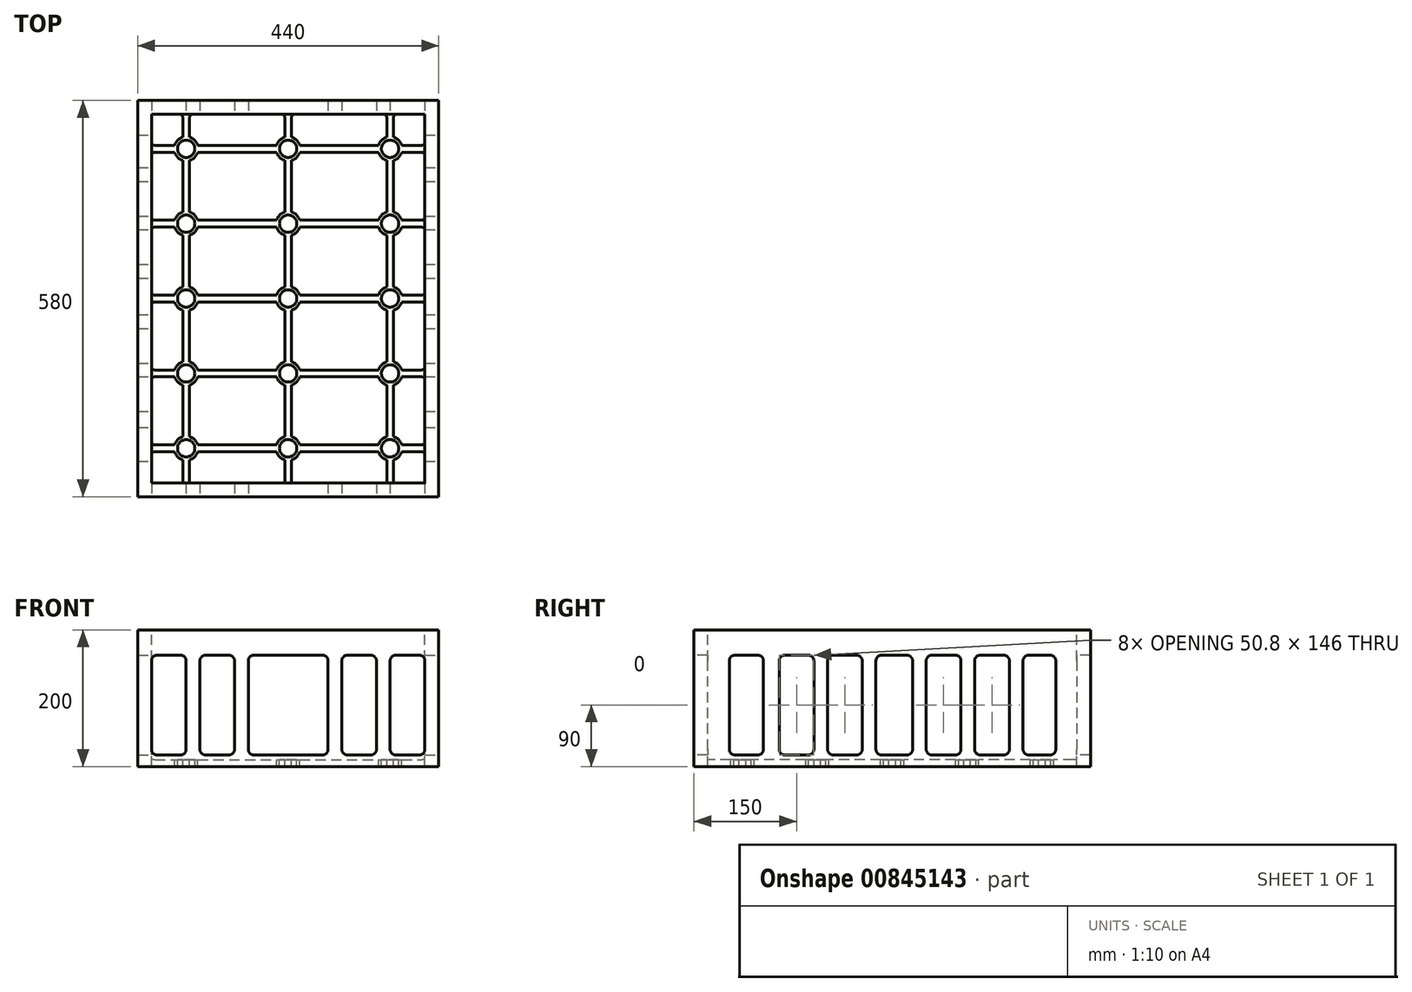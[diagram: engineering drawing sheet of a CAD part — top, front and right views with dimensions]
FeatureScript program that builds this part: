
annotation { "Feature Type Name" : "Feature", "Feature Type Description" : "" }
export const myFeature = defineFeature(function(context is Context, id is Id, definition is map)
    precondition{}
    {
        {
            var Q0;
            Q0=qCreatedBy(makeId("Top.planeOp"),FACE);
            var sketch = newSketch(context, id + "F0", { "sketchPlane" : qUnion([Q0])});
            skLineSegment(sketch, "E0.bottom", {"start": v(0, 0) * mm, "end": v(440, 0) * mm});
            skLineSegment(sketch, "E0.top", {"start": v(0, 580) * mm, "end": v(440, 580) * mm});
            skLineSegment(sketch, "E0.left", {"start": v(0, 0) * mm, "end": v(0, 580) * mm});
            skLineSegment(sketch, "E0.right", {"start": v(440, 0) * mm, "end": v(440, 580) * mm});
            skSolve(sketch);
        }
        {
            var Q0;
            Q0 = qSketchRegion(id + "F0", true);
            extrude(context, id + "F1", {"entities" : qUnion([Q0]), "depth" : 200 * mm, "offsetDistance" : 25 * mm});
        }
        {
            var Q0;
            Q0=makeQuery(id+"F1.opExtrude","CAP_FACE",FACE,{"disambiguationData":[OSD([sQuery(id+"F0.wireOp",EDGE,"E0.bottom"),sQuery(id+"F0.wireOp",EDGE,"E0.top"),sQuery(id+"F0.wireOp",EDGE,"E0.left"),sQuery(id+"F0.wireOp",EDGE,"E0.right")])],"isStart":false});
            var sketch = newSketch(context, id + "F2", { "sketchPlane" : qUnion([Q0])});
            skLineSegment(sketch, "E1.left", {"start": v(0, 0) * mm, "end": v(0, 0) * mm});
            skLineSegment(sketch, "E2.bottom", {"start": v(20, 20) * mm, "end": v(420, 20) * mm});
            skLineSegment(sketch, "E2.top", {"start": v(20, 560) * mm, "end": v(420, 560) * mm});
            skLineSegment(sketch, "E2.left", {"start": v(20, 20) * mm, "end": v(20, 560) * mm});
            skLineSegment(sketch, "E2.right", {"start": v(420, 20) * mm, "end": v(420, 560) * mm});
            skSolve(sketch);
        }
        {
            var Q0;
            Q0=makeQuery(id+"F2.imprint","IMPRINT",FACE,{"disambiguationData":[TD([[makeQuery(id+"F2.imprint","IMPRINT",EDGE,{"derivedFrom":sQuery(id+"F2.wireOp",EDGE,"E2.bottom")}),1.0]])]});
            extrude(context, id + "F3", {"entities" : qUnion([Q0]), "operationType" : NewBodyOperationType.REMOVE, "oppositeDirection" : true, "depth" : 190 * mm, "offsetDistance" : 25 * mm});
        }
        {
            var Q0;
            Q0=makeQuery(id+"F3.boolean.opBoolean","COPY",FACE,{"derivedFrom":makeQuery(id+"F3.opExtrude","CAP_FACE",FACE,{"disambiguationData":[OSD([sQuery(id+"F2.wireOp",EDGE,"E2.bottom"),sQuery(id+"F2.wireOp",EDGE,"E2.top"),sQuery(id+"F2.wireOp",EDGE,"E2.left"),sQuery(id+"F2.wireOp",EDGE,"E2.right")])],"isStart":false})});
            var sketch = newSketch(context, id + "F4", { "sketchPlane" : qUnion([Q0])});
            skCircle(sketch, "E3", {"center": v(70.8, 509.2) * mm, "radius": 12.7 * mm});
            skCircle(sketch, "E4", {"center": v(70.8, 509.2) * mm, "radius": 17.7 * mm});
            skCircle(sketch, "E5.1.0.0", {"center": v(220, 509.2) * mm, "radius": 17.7 * mm});
            skCircle(sketch, "E5.1.0.1", {"center": v(220, 509.2) * mm, "radius": 12.7 * mm});
            skCircle(sketch, "E5.2.0.0", {"center": v(369.2, 509.2) * mm, "radius": 17.7 * mm});
            skCircle(sketch, "E5.2.0.1", {"center": v(369.2, 509.2) * mm, "radius": 12.7 * mm});
            skCircle(sketch, "E6.0.1.0", {"center": v(369.2, 399.6) * mm, "radius": 17.7 * mm});
            skCircle(sketch, "E6.0.1.1", {"center": v(70.8, 399.6) * mm, "radius": 12.7 * mm});
            skCircle(sketch, "E6.0.1.2", {"center": v(369.2, 399.6) * mm, "radius": 12.7 * mm});
            skArc(sketch, "E6.0.1.3", {"start": v(87.78, 404.6) * mm, "mid": v(53.1, 399.6) * mm, "end": v(87.78, 394.6) * mm});
            skCircle(sketch, "E6.0.1.4", {"center": v(220, 399.6) * mm, "radius": 17.7 * mm});
            skCircle(sketch, "E6.0.1.5", {"center": v(220, 399.6) * mm, "radius": 12.7 * mm});
            skCircle(sketch, "E6.0.2.0", {"center": v(369.2, 290) * mm, "radius": 17.7 * mm});
            skCircle(sketch, "E6.0.2.1", {"center": v(70.8, 290) * mm, "radius": 12.7 * mm});
            skCircle(sketch, "E6.0.2.2", {"center": v(369.2, 290) * mm, "radius": 12.7 * mm});
            skCircle(sketch, "E6.0.2.3", {"center": v(70.8, 290) * mm, "radius": 17.7 * mm});
            skCircle(sketch, "E6.0.2.4", {"center": v(220, 290) * mm, "radius": 17.7 * mm});
            skCircle(sketch, "E6.0.2.5", {"center": v(220, 290) * mm, "radius": 12.7 * mm});
            skCircle(sketch, "E6.0.3.0", {"center": v(369.2, 180.4) * mm, "radius": 17.7 * mm});
            skCircle(sketch, "E6.0.3.1", {"center": v(70.8, 180.4) * mm, "radius": 12.7 * mm});
            skCircle(sketch, "E6.0.3.2", {"center": v(369.2, 180.4) * mm, "radius": 12.7 * mm});
            skCircle(sketch, "E6.0.3.3", {"center": v(70.8, 180.4) * mm, "radius": 17.7 * mm});
            skCircle(sketch, "E6.0.3.4", {"center": v(220, 180.4) * mm, "radius": 17.7 * mm});
            skCircle(sketch, "E6.0.3.5", {"center": v(220, 180.4) * mm, "radius": 12.7 * mm});
            skCircle(sketch, "E6.0.4.0", {"center": v(369.2, 70.8) * mm, "radius": 17.7 * mm});
            skCircle(sketch, "E6.0.4.1", {"center": v(70.8, 70.8) * mm, "radius": 12.7 * mm});
            skCircle(sketch, "E6.0.4.2", {"center": v(369.2, 70.8) * mm, "radius": 12.7 * mm});
            skCircle(sketch, "E6.0.4.3", {"center": v(70.8, 70.8) * mm, "radius": 17.7 * mm});
            skCircle(sketch, "E6.0.4.4", {"center": v(220, 70.8) * mm, "radius": 17.7 * mm});
            skCircle(sketch, "E6.0.4.5", {"center": v(220, 70.8) * mm, "radius": 12.7 * mm});
            skLineSegment(sketch, "E7.0", {"start": v(25, 504.2) * mm, "end": v(53.82, 504.2) * mm});
            skLineSegment(sketch, "E8.0", {"start": v(25, 514.2) * mm, "end": v(53.82, 514.2) * mm});
            skLineSegment(sketch, "E9.bottom", {"start": v(20, 20) * mm, "end": v(420, 20) * mm});
            skLineSegment(sketch, "E9.top", {"start": v(80.8, 560) * mm, "end": v(210, 560) * mm});
            skLineSegment(sketch, "E9.left", {"start": v(20, 519.2) * mm, "end": v(20, 560) * mm});
            skLineSegment(sketch, "E9.right", {"start": v(420, 409.6) * mm, "end": v(420, 499.2) * mm});
            skArc(sketch, "E10.filletArc", {"start": v(20, 519.2) * mm, "mid": v(21.46, 515.66) * mm, "end": v(25, 514.2) * mm});
            skLineSegment(sketch, "E11", {"start": v(20, 389.6) * mm, "end": v(20, 300) * mm});
            skPoint(sketch, "E12.visualSharp", {"position": v(20, 504.2) * mm});
            skArc(sketch, "E12.filletArc", {"start": v(25, 504.2) * mm, "mid": v(21.46, 502.74) * mm, "end": v(20, 499.2) * mm});
            skLineSegment(sketch, "E13.0", {"start": v(65.8, 555) * mm, "end": v(65.8, 526.18) * mm});
            skLineSegment(sketch, "E14.0", {"start": v(75.8, 555) * mm, "end": v(75.8, 526.18) * mm});
            skLineSegment(sketch, "E15", {"start": v(20, 560) * mm, "end": v(60.8, 560) * mm});
            skArc(sketch, "E16.filletArc", {"start": v(80.8, 560) * mm, "mid": v(77.26, 558.54) * mm, "end": v(75.8, 555) * mm});
            skArc(sketch, "E17.filletArc", {"start": v(65.8, 555) * mm, "mid": v(64.34, 558.54) * mm, "end": v(60.8, 560) * mm});
            skLineSegment(sketch, "E18.trimOffspring", {"start": v(87.78, 514.2) * mm, "end": v(203.02, 514.2) * mm});
            skLineSegment(sketch, "E19.trimOffspring", {"start": v(87.78, 504.2) * mm, "end": v(203.02, 504.2) * mm});
            skLineSegment(sketch, "E20.trimOffspring", {"start": v(65.8, 492.22) * mm, "end": v(65.8, 416.58) * mm});
            skLineSegment(sketch, "E21.trimOffspring", {"start": v(75.8, 492.22) * mm, "end": v(75.8, 416.58) * mm});
            skLineSegment(sketch, "E22.0", {"start": v(215, 555) * mm, "end": v(215, 526.18) * mm});
            skLineSegment(sketch, "E23.0", {"start": v(225, 555) * mm, "end": v(225, 526.18) * mm});
            skLineSegment(sketch, "E24.0", {"start": v(364.2, 555) * mm, "end": v(364.2, 526.18) * mm});
            skLineSegment(sketch, "E25.0", {"start": v(374.2, 555) * mm, "end": v(374.2, 526.18) * mm});
            skArc(sketch, "E26.filletArc", {"start": v(215, 555) * mm, "mid": v(213.54, 558.54) * mm, "end": v(210, 560) * mm});
            skLineSegment(sketch, "E27", {"start": v(379.2, 560) * mm, "end": v(420, 560) * mm});
            skPoint(sketch, "E28.visualSharp", {"position": v(225, 560) * mm});
            skArc(sketch, "E28.filletArc", {"start": v(230, 560) * mm, "mid": v(226.46, 558.54) * mm, "end": v(225, 555) * mm});
            skArc(sketch, "E29.filletArc", {"start": v(379.2, 560) * mm, "mid": v(375.66, 558.54) * mm, "end": v(374.2, 555) * mm});
            skLineSegment(sketch, "E30", {"start": v(230, 560) * mm, "end": v(359.2, 560) * mm});
            skPoint(sketch, "E31.visualSharp", {"position": v(364.2, 560) * mm});
            skArc(sketch, "E31.filletArc", {"start": v(364.2, 555) * mm, "mid": v(362.74, 558.54) * mm, "end": v(359.2, 560) * mm});
            skArc(sketch, "E32.filletArc", {"start": v(420, 499.2) * mm, "mid": v(418.54, 502.74) * mm, "end": v(415, 504.2) * mm});
            skLineSegment(sketch, "E33", {"start": v(420, 560) * mm, "end": v(420, 519.2) * mm});
            skPoint(sketch, "E34.visualSharp", {"position": v(420, 514.2) * mm});
            skArc(sketch, "E34.filletArc", {"start": v(415, 514.2) * mm, "mid": v(418.54, 515.66) * mm, "end": v(420, 519.2) * mm});
            skLineSegment(sketch, "E35.0", {"start": v(25, 394.6) * mm, "end": v(53.82, 394.6) * mm});
            skLineSegment(sketch, "E36.0", {"start": v(25, 404.6) * mm, "end": v(53.82, 404.6) * mm});
            skArc(sketch, "E37.filletArc", {"start": v(25, 394.6) * mm, "mid": v(21.46, 393.14) * mm, "end": v(20, 389.6) * mm});
            skLineSegment(sketch, "E38", {"start": v(20, 499.2) * mm, "end": v(20, 409.6) * mm});
            skPoint(sketch, "E39.visualSharp", {"position": v(20, 404.6) * mm});
            skArc(sketch, "E39.filletArc", {"start": v(20, 409.6) * mm, "mid": v(21.46, 406.06) * mm, "end": v(25, 404.6) * mm});
            skArc(sketch, "E40.filletArc", {"start": v(415, 404.6) * mm, "mid": v(418.54, 406.06) * mm, "end": v(420, 409.6) * mm});
            skLineSegment(sketch, "E41", {"start": v(420, 389.6) * mm, "end": v(420, 300) * mm});
            skPoint(sketch, "E42.visualSharp", {"position": v(420, 394.6) * mm});
            skArc(sketch, "E42.filletArc", {"start": v(420, 389.6) * mm, "mid": v(418.54, 393.14) * mm, "end": v(415, 394.6) * mm});
            skLineSegment(sketch, "E43.trimOffspring", {"start": v(215, 492.22) * mm, "end": v(215, 416.58) * mm});
            skLineSegment(sketch, "E44.trimOffspring", {"start": v(225, 492.22) * mm, "end": v(225, 416.58) * mm});
            skLineSegment(sketch, "E45.trimOffspring", {"start": v(236.98, 504.2) * mm, "end": v(352.22, 504.2) * mm});
            skLineSegment(sketch, "E46.trimOffspring", {"start": v(236.98, 514.2) * mm, "end": v(352.22, 514.2) * mm});
            skLineSegment(sketch, "E47.trimOffspring", {"start": v(364.2, 492.22) * mm, "end": v(364.2, 416.58) * mm});
            skLineSegment(sketch, "E48.trimOffspring", {"start": v(374.2, 492.22) * mm, "end": v(374.2, 416.58) * mm});
            skLineSegment(sketch, "E49.trimOffspring", {"start": v(386.18, 504.2) * mm, "end": v(415, 504.2) * mm});
            skLineSegment(sketch, "E50.trimOffspring", {"start": v(386.18, 514.2) * mm, "end": v(415, 514.2) * mm});
            skLineSegment(sketch, "E51.trimOffspring", {"start": v(87.78, 404.6) * mm, "end": v(203.02, 404.6) * mm});
            skLineSegment(sketch, "E52.trimOffspring", {"start": v(87.78, 394.6) * mm, "end": v(203.02, 394.6) * mm});
            skLineSegment(sketch, "E53.trimOffspring", {"start": v(75.8, 382.62) * mm, "end": v(75.8, 306.98) * mm});
            skLineSegment(sketch, "E54.trimOffspring", {"start": v(65.8, 382.62) * mm, "end": v(65.8, 306.98) * mm});
            skLineSegment(sketch, "E55.trimOffspring", {"start": v(215, 382.62) * mm, "end": v(215, 306.98) * mm});
            skLineSegment(sketch, "E56.trimOffspring", {"start": v(225, 382.62) * mm, "end": v(225, 306.98) * mm});
            skLineSegment(sketch, "E57.trimOffspring", {"start": v(236.98, 394.6) * mm, "end": v(352.22, 394.6) * mm});
            skLineSegment(sketch, "E58.trimOffspring", {"start": v(236.98, 404.6) * mm, "end": v(352.22, 404.6) * mm});
            skLineSegment(sketch, "E59.trimOffspring", {"start": v(364.2, 382.62) * mm, "end": v(364.2, 306.98) * mm});
            skLineSegment(sketch, "E60.trimOffspring", {"start": v(374.2, 382.62) * mm, "end": v(374.2, 306.98) * mm});
            skLineSegment(sketch, "E61.trimOffspring", {"start": v(386.18, 394.6) * mm, "end": v(415, 394.6) * mm});
            skLineSegment(sketch, "E62.trimOffspring", {"start": v(386.18, 404.6) * mm, "end": v(415, 404.6) * mm});
            skLineSegment(sketch, "E63.0", {"start": v(25, 285) * mm, "end": v(53.82, 285) * mm});
            skLineSegment(sketch, "E64.0", {"start": v(25, 295) * mm, "end": v(53.82, 295) * mm});
            skArc(sketch, "E65.filletArc", {"start": v(20, 300) * mm, "mid": v(21.46, 296.46) * mm, "end": v(25, 295) * mm});
            skArc(sketch, "E66.filletArc", {"start": v(415, 295) * mm, "mid": v(418.54, 296.46) * mm, "end": v(420, 300) * mm});
            skLineSegment(sketch, "E67", {"start": v(20, 280) * mm, "end": v(20, 190.4) * mm});
            skLineSegment(sketch, "E68", {"start": v(420, 280) * mm, "end": v(420, 190.4) * mm});
            skPoint(sketch, "E69.visualSharp", {"position": v(20, 285) * mm});
            skArc(sketch, "E69.filletArc", {"start": v(25, 285) * mm, "mid": v(21.46, 283.54) * mm, "end": v(20, 280) * mm});
            skPoint(sketch, "E70.visualSharp", {"position": v(420, 285) * mm});
            skArc(sketch, "E70.filletArc", {"start": v(420, 280) * mm, "mid": v(418.54, 283.54) * mm, "end": v(415, 285) * mm});
            skLineSegment(sketch, "E71.trimOffspring", {"start": v(65.8, 273.02) * mm, "end": v(65.8, 197.38) * mm});
            skLineSegment(sketch, "E72.trimOffspring", {"start": v(75.8, 273.02) * mm, "end": v(75.8, 197.38) * mm});
            skLineSegment(sketch, "E73.trimOffspring", {"start": v(87.78, 285) * mm, "end": v(203.02, 285) * mm});
            skLineSegment(sketch, "E74.trimOffspring", {"start": v(87.78, 295) * mm, "end": v(203.02, 295) * mm});
            skLineSegment(sketch, "E75.trimOffspring", {"start": v(215, 273.02) * mm, "end": v(215, 197.38) * mm});
            skLineSegment(sketch, "E76.trimOffspring", {"start": v(225, 273.02) * mm, "end": v(225, 197.38) * mm});
            skLineSegment(sketch, "E77.trimOffspring", {"start": v(236.98, 285) * mm, "end": v(352.22, 285) * mm});
            skLineSegment(sketch, "E78.trimOffspring", {"start": v(236.98, 295) * mm, "end": v(352.22, 295) * mm});
            skLineSegment(sketch, "E79.trimOffspring", {"start": v(364.2, 273.02) * mm, "end": v(364.2, 197.38) * mm});
            skLineSegment(sketch, "E80.trimOffspring", {"start": v(374.2, 273.02) * mm, "end": v(374.2, 197.38) * mm});
            skLineSegment(sketch, "E81.trimOffspring", {"start": v(386.18, 285) * mm, "end": v(415, 285) * mm});
            skLineSegment(sketch, "E82.trimOffspring", {"start": v(386.18, 295) * mm, "end": v(415, 295) * mm});
            skLineSegment(sketch, "E83.0", {"start": v(25, 175.4) * mm, "end": v(53.82, 175.4) * mm});
            skLineSegment(sketch, "E84.0", {"start": v(25, 185.4) * mm, "end": v(53.82, 185.4) * mm});
            skArc(sketch, "E85.filletArc", {"start": v(20, 190.4) * mm, "mid": v(21.46, 186.86) * mm, "end": v(25, 185.4) * mm});
            skArc(sketch, "E86.filletArc", {"start": v(415, 185.4) * mm, "mid": v(418.54, 186.86) * mm, "end": v(420, 190.4) * mm});
            skLineSegment(sketch, "E87", {"start": v(20, 170.4) * mm, "end": v(20, 80.8) * mm});
            skLineSegment(sketch, "E88", {"start": v(420, 170.4) * mm, "end": v(420, 80.8) * mm});
            skPoint(sketch, "E89.visualSharp", {"position": v(20, 175.4) * mm});
            skArc(sketch, "E89.filletArc", {"start": v(25, 175.4) * mm, "mid": v(21.46, 173.94) * mm, "end": v(20, 170.4) * mm});
            skPoint(sketch, "E90.visualSharp", {"position": v(420, 175.4) * mm});
            skArc(sketch, "E90.filletArc", {"start": v(420, 170.4) * mm, "mid": v(418.54, 173.94) * mm, "end": v(415, 175.4) * mm});
            skLineSegment(sketch, "E91.trimOffspring", {"start": v(75.8, 163.42) * mm, "end": v(75.8, 87.78) * mm});
            skLineSegment(sketch, "E92.trimOffspring", {"start": v(65.8, 163.42) * mm, "end": v(65.8, 87.78) * mm});
            skLineSegment(sketch, "E93.trimOffspring", {"start": v(87.78, 175.4) * mm, "end": v(203.02, 175.4) * mm});
            skLineSegment(sketch, "E94.trimOffspring", {"start": v(87.78, 185.4) * mm, "end": v(203.02, 185.4) * mm});
            skLineSegment(sketch, "E95.trimOffspring", {"start": v(215, 163.42) * mm, "end": v(215, 87.78) * mm});
            skLineSegment(sketch, "E96.trimOffspring", {"start": v(225, 163.42) * mm, "end": v(225, 87.78) * mm});
            skLineSegment(sketch, "E97.trimOffspring", {"start": v(236.98, 175.4) * mm, "end": v(352.22, 175.4) * mm});
            skLineSegment(sketch, "E98.trimOffspring", {"start": v(236.98, 185.4) * mm, "end": v(352.22, 185.4) * mm});
            skLineSegment(sketch, "E99.trimOffspring", {"start": v(364.2, 163.42) * mm, "end": v(364.2, 87.78) * mm});
            skLineSegment(sketch, "E100.trimOffspring", {"start": v(374.2, 163.42) * mm, "end": v(374.2, 87.78) * mm});
            skLineSegment(sketch, "E101.trimOffspring", {"start": v(386.18, 175.4) * mm, "end": v(415, 175.4) * mm});
            skLineSegment(sketch, "E102.trimOffspring", {"start": v(386.18, 185.4) * mm, "end": v(415, 185.4) * mm});
            skLineSegment(sketch, "E103.0", {"start": v(25, 65.8) * mm, "end": v(53.82, 65.8) * mm});
            skLineSegment(sketch, "E104.0", {"start": v(25, 75.8) * mm, "end": v(53.82, 75.8) * mm});
            skArc(sketch, "E105.filletArc", {"start": v(20, 80.8) * mm, "mid": v(21.46, 77.26) * mm, "end": v(25, 75.8) * mm});
            skArc(sketch, "E106.filletArc", {"start": v(415, 75.8) * mm, "mid": v(418.54, 77.26) * mm, "end": v(420, 80.8) * mm});
            skLineSegment(sketch, "E107", {"start": v(20, 60.8) * mm, "end": v(20, 20) * mm});
            skLineSegment(sketch, "E108", {"start": v(420, 60.8) * mm, "end": v(420, 20) * mm});
            skPoint(sketch, "E109.visualSharp", {"position": v(20, 65.8) * mm});
            skArc(sketch, "E109.filletArc", {"start": v(25, 65.8) * mm, "mid": v(21.46, 64.34) * mm, "end": v(20, 60.8) * mm});
            skPoint(sketch, "E110.visualSharp", {"position": v(420, 65.8) * mm});
            skArc(sketch, "E110.filletArc", {"start": v(420, 60.8) * mm, "mid": v(418.54, 64.34) * mm, "end": v(415, 65.8) * mm});
            skLineSegment(sketch, "E111.trimOffspring", {"start": v(65.8, 53.82) * mm, "end": v(65.8, 20) * mm});
            skLineSegment(sketch, "E112.trimOffspring", {"start": v(75.8, 53.82) * mm, "end": v(75.8, 20) * mm});
            skLineSegment(sketch, "E113.trimOffspring", {"start": v(87.78, 65.8) * mm, "end": v(203.02, 65.8) * mm});
            skLineSegment(sketch, "E114.trimOffspring", {"start": v(87.78, 75.8) * mm, "end": v(203.02, 75.8) * mm});
            skLineSegment(sketch, "E115.trimOffspring", {"start": v(215, 53.82) * mm, "end": v(215, 20) * mm});
            skLineSegment(sketch, "E116.trimOffspring", {"start": v(225, 53.82) * mm, "end": v(225, 20) * mm});
            skLineSegment(sketch, "E117.trimOffspring", {"start": v(236.98, 65.8) * mm, "end": v(352.22, 65.8) * mm});
            skLineSegment(sketch, "E118.trimOffspring", {"start": v(236.98, 75.8) * mm, "end": v(352.22, 75.8) * mm});
            skLineSegment(sketch, "E119.trimOffspring", {"start": v(364.2, 53.82) * mm, "end": v(364.2, 20) * mm});
            skLineSegment(sketch, "E120.trimOffspring", {"start": v(374.2, 53.82) * mm, "end": v(374.2, 20) * mm});
            skLineSegment(sketch, "E121.trimOffspring", {"start": v(386.18, 65.8) * mm, "end": v(415, 65.8) * mm});
            skLineSegment(sketch, "E122.trimOffspring", {"start": v(386.18, 75.8) * mm, "end": v(415, 75.8) * mm});
            skSolve(sketch);
        }
        {
            var Q0;
            {var subQ0=sQuery(id+"F4.wireOp",EDGE,"E8.0");Q0=makeQuery(id+"F4.imprint","IMPRINT",FACE,{"disambiguationData":[TD([[makeQuery(id+"F4.imprint","IMPRINT",EDGE,{"derivedFrom":subQ0}),1.0]])]});}
            var Q1;
            Q1=makeQuery(id+"F4.imprint","IMPRINT",FACE,{"disambiguationData":[TD([[makeQuery(id+"F4.imprint","IMPRINT",EDGE,{"derivedFrom":sQuery(id+"F4.wireOp",EDGE,"E9.top")}),-1.0]])]});
            var Q2;
            {var subQ3=sQuery(id+"F4.wireOp",EDGE,"E23.0");Q2=makeQuery(id+"F4.imprint","IMPRINT",FACE,{"disambiguationData":[TD([[makeQuery(id+"F4.imprint","IMPRINT",EDGE,{"derivedFrom":subQ3}),1.0]])]});}
            var Q3;
            {var subQ0=sQuery(id+"F4.wireOp",EDGE,"E25.0");Q3=makeQuery(id+"F4.imprint","IMPRINT",FACE,{"disambiguationData":[TD([[makeQuery(id+"F4.imprint","IMPRINT",EDGE,{"derivedFrom":subQ0}),1.0]])]});}
            var Q4;
            {var subQ0=sQuery(id+"F4.wireOp",EDGE,"E7.0");Q4=makeQuery(id+"F4.imprint","IMPRINT",FACE,{"disambiguationData":[TD([[makeQuery(id+"F4.imprint","IMPRINT",EDGE,{"derivedFrom":subQ0}),-1.0]])]});}
            var Q5;
            {var subQ3=sQuery(id+"F4.wireOp",EDGE,"E19.trimOffspring");Q5=makeQuery(id+"F4.imprint","IMPRINT",FACE,{"disambiguationData":[TD([[makeQuery(id+"F4.imprint","IMPRINT",EDGE,{"derivedFrom":subQ3}),-1.0]])]});}
            var Q6;
            {var subQ0=sQuery(id+"F4.wireOp",EDGE,"E44.trimOffspring");Q6=makeQuery(id+"F4.imprint","IMPRINT",FACE,{"disambiguationData":[TD([[makeQuery(id+"F4.imprint","IMPRINT",EDGE,{"derivedFrom":subQ0}),1.0]])]});}
            var Q7;
            Q7=makeQuery(id+"F4.imprint","IMPRINT",FACE,{"disambiguationData":[TD([[makeQuery(id+"F4.imprint","IMPRINT",EDGE,{"derivedFrom":sQuery(id+"F4.wireOp",EDGE,"E9.right")}),1.0]])]});
            var Q8;
            Q8=makeQuery(id+"F4.imprint","IMPRINT",FACE,{"disambiguationData":[TD([[makeQuery(id+"F4.imprint","IMPRINT",EDGE,{"derivedFrom":sQuery(id+"F4.wireOp",EDGE,"E11")}),-1.0]])]});
            var Q9;
            {var subQ5=sQuery(id+"F4.wireOp",EDGE,"E52.trimOffspring");Q9=makeQuery(id+"F4.imprint","IMPRINT",FACE,{"disambiguationData":[TD([[makeQuery(id+"F4.imprint","IMPRINT",EDGE,{"derivedFrom":subQ5}),-1.0]])]});}
            var Q10;
            {var subQ3=sQuery(id+"F4.wireOp",EDGE,"E56.trimOffspring");Q10=makeQuery(id+"F4.imprint","IMPRINT",FACE,{"disambiguationData":[TD([[makeQuery(id+"F4.imprint","IMPRINT",EDGE,{"derivedFrom":subQ3}),1.0]])]});}
            var Q11;
            Q11=makeQuery(id+"F4.imprint","IMPRINT",FACE,{"disambiguationData":[TD([[makeQuery(id+"F4.imprint","IMPRINT",EDGE,{"derivedFrom":sQuery(id+"F4.wireOp",EDGE,"E41")}),1.0]])]});
            var Q12;
            {var subQ0=sQuery(id+"F4.wireOp",EDGE,"E63.0");Q12=makeQuery(id+"F4.imprint","IMPRINT",FACE,{"disambiguationData":[TD([[makeQuery(id+"F4.imprint","IMPRINT",EDGE,{"derivedFrom":subQ0}),-1.0]])]});}
            var Q13;
            {var subQ3=sQuery(id+"F4.wireOp",EDGE,"E72.trimOffspring");Q13=makeQuery(id+"F4.imprint","IMPRINT",FACE,{"disambiguationData":[TD([[makeQuery(id+"F4.imprint","IMPRINT",EDGE,{"derivedFrom":subQ3}),1.0]])]});}
            var Q14;
            {var subQ0=sQuery(id+"F4.wireOp",EDGE,"E76.trimOffspring");Q14=makeQuery(id+"F4.imprint","IMPRINT",FACE,{"disambiguationData":[TD([[makeQuery(id+"F4.imprint","IMPRINT",EDGE,{"derivedFrom":subQ0}),1.0]])]});}
            var Q15;
            Q15=makeQuery(id+"F4.imprint","IMPRINT",FACE,{"disambiguationData":[TD([[makeQuery(id+"F4.imprint","IMPRINT",EDGE,{"derivedFrom":sQuery(id+"F4.wireOp",EDGE,"E68")}),1.0]])]});
            var Q16;
            {var subQ0=sQuery(id+"F4.wireOp",EDGE,"E83.0");Q16=makeQuery(id+"F4.imprint","IMPRINT",FACE,{"disambiguationData":[TD([[makeQuery(id+"F4.imprint","IMPRINT",EDGE,{"derivedFrom":subQ0}),-1.0]])]});}
            var Q17;
            {var subQ3=sQuery(id+"F4.wireOp",EDGE,"E91.trimOffspring");Q17=makeQuery(id+"F4.imprint","IMPRINT",FACE,{"disambiguationData":[TD([[makeQuery(id+"F4.imprint","IMPRINT",EDGE,{"derivedFrom":subQ3}),1.0]])]});}
            var Q18;
            {var subQ0=sQuery(id+"F4.wireOp",EDGE,"E96.trimOffspring");Q18=makeQuery(id+"F4.imprint","IMPRINT",FACE,{"disambiguationData":[TD([[makeQuery(id+"F4.imprint","IMPRINT",EDGE,{"derivedFrom":subQ0}),1.0]])]});}
            var Q19;
            Q19=makeQuery(id+"F4.imprint","IMPRINT",FACE,{"disambiguationData":[TD([[makeQuery(id+"F4.imprint","IMPRINT",EDGE,{"derivedFrom":sQuery(id+"F4.wireOp",EDGE,"E88")}),1.0]])]});
            var Q20;
            {var subQ1=sQuery(id+"F4.wireOp",EDGE,"E103.0");Q20=makeQuery(id+"F4.imprint","IMPRINT",FACE,{"disambiguationData":[TD([[makeQuery(id+"F4.imprint","IMPRINT",EDGE,{"derivedFrom":subQ1}),-1.0]])]});}
            var Q21;
            {var subQ3=sQuery(id+"F4.wireOp",EDGE,"E112.trimOffspring");Q21=makeQuery(id+"F4.imprint","IMPRINT",FACE,{"disambiguationData":[TD([[makeQuery(id+"F4.imprint","IMPRINT",EDGE,{"derivedFrom":subQ3}),1.0]])]});}
            var Q22;
            {var subQ0=sQuery(id+"F4.wireOp",EDGE,"E116.trimOffspring");Q22=makeQuery(id+"F4.imprint","IMPRINT",FACE,{"disambiguationData":[TD([[makeQuery(id+"F4.imprint","IMPRINT",EDGE,{"derivedFrom":subQ0}),1.0]])]});}
            var Q23;
            {var subQ1=sQuery(id+"F4.wireOp",EDGE,"E108");Q23=makeQuery(id+"F4.imprint","IMPRINT",FACE,{"disambiguationData":[TD([[makeQuery(id+"F4.imprint","IMPRINT",EDGE,{"derivedFrom":subQ1}),1.0]])]});}
            var Q24;
            Q24=makeQuery(id+"F1.opExtrude","CAP_FACE",FACE,{"disambiguationData":[OSD([sQuery(id+"F0.wireOp",EDGE,"E0.bottom"),sQuery(id+"F0.wireOp",EDGE,"E0.top"),sQuery(id+"F0.wireOp",EDGE,"E0.left"),sQuery(id+"F0.wireOp",EDGE,"E0.right")])],"isStart":true});
            extrude(context, id + "F5", {"entities" : qUnion([Q0, Q1, Q2, Q3, Q4, Q5, Q6, Q7, Q8, Q9, Q10, Q11, Q12, Q13, Q14, Q15, Q16, Q17, Q18, Q19, Q20, Q21, Q22, Q23]), "operationType" : NewBodyOperationType.REMOVE, "endBound" : BoundingType.UP_TO_SURFACE, "oppositeDirection" : true, "depth" : 25 * mm, "endBoundEntityFace" : qUnion([Q24]), "offsetDistance" : 25 * mm});
        }
        {
            var Q0;
            Q0=makeQuery(id+"F4.imprint","IMPRINT",FACE,{"disambiguationData":[TD([[makeQuery(id+"F4.imprint","IMPRINT",EDGE,{"derivedFrom":sQuery(id+"F4.wireOp",EDGE,"E3")}),1.0]])]});
            var Q1;
            Q1=makeQuery(id+"F4.imprint","IMPRINT",FACE,{"disambiguationData":[TD([[makeQuery(id+"F4.imprint","IMPRINT",EDGE,{"derivedFrom":sQuery(id+"F4.wireOp",EDGE,"E6.0.1.1")}),1.0]])]});
            var Q2;
            Q2=makeQuery(id+"F4.imprint","IMPRINT",FACE,{"disambiguationData":[TD([[makeQuery(id+"F4.imprint","IMPRINT",EDGE,{"derivedFrom":sQuery(id+"F4.wireOp",EDGE,"E6.0.2.1")}),1.0]])]});
            var Q3;
            Q3=makeQuery(id+"F4.imprint","IMPRINT",FACE,{"disambiguationData":[TD([[makeQuery(id+"F4.imprint","IMPRINT",EDGE,{"derivedFrom":sQuery(id+"F4.wireOp",EDGE,"E6.0.3.1")}),1.0]])]});
            var Q4;
            Q4=makeQuery(id+"F4.imprint","IMPRINT",FACE,{"disambiguationData":[TD([[makeQuery(id+"F4.imprint","IMPRINT",EDGE,{"derivedFrom":sQuery(id+"F4.wireOp",EDGE,"E6.0.4.1")}),1.0]])]});
            var Q5;
            Q5=makeQuery(id+"F4.imprint","IMPRINT",FACE,{"disambiguationData":[TD([[makeQuery(id+"F4.imprint","IMPRINT",EDGE,{"derivedFrom":sQuery(id+"F4.wireOp",EDGE,"E5.1.0.1")}),1.0]])]});
            var Q6;
            Q6=makeQuery(id+"F4.imprint","IMPRINT",FACE,{"disambiguationData":[TD([[makeQuery(id+"F4.imprint","IMPRINT",EDGE,{"derivedFrom":sQuery(id+"F4.wireOp",EDGE,"E6.0.1.5")}),1.0]])]});
            var Q7;
            Q7=makeQuery(id+"F4.imprint","IMPRINT",FACE,{"disambiguationData":[TD([[makeQuery(id+"F4.imprint","IMPRINT",EDGE,{"derivedFrom":sQuery(id+"F4.wireOp",EDGE,"E6.0.2.5")}),1.0]])]});
            var Q8;
            Q8=makeQuery(id+"F4.imprint","IMPRINT",FACE,{"disambiguationData":[TD([[makeQuery(id+"F4.imprint","IMPRINT",EDGE,{"derivedFrom":sQuery(id+"F4.wireOp",EDGE,"E6.0.3.5")}),1.0]])]});
            var Q9;
            Q9=makeQuery(id+"F4.imprint","IMPRINT",FACE,{"disambiguationData":[TD([[makeQuery(id+"F4.imprint","IMPRINT",EDGE,{"derivedFrom":sQuery(id+"F4.wireOp",EDGE,"E6.0.4.5")}),1.0]])]});
            var Q10;
            Q10=makeQuery(id+"F4.imprint","IMPRINT",FACE,{"disambiguationData":[TD([[makeQuery(id+"F4.imprint","IMPRINT",EDGE,{"derivedFrom":sQuery(id+"F4.wireOp",EDGE,"E6.0.4.2")}),1.0]])]});
            var Q11;
            Q11=makeQuery(id+"F4.imprint","IMPRINT",FACE,{"disambiguationData":[TD([[makeQuery(id+"F4.imprint","IMPRINT",EDGE,{"derivedFrom":sQuery(id+"F4.wireOp",EDGE,"E6.0.3.2")}),1.0]])]});
            var Q12;
            Q12=makeQuery(id+"F4.imprint","IMPRINT",FACE,{"disambiguationData":[TD([[makeQuery(id+"F4.imprint","IMPRINT",EDGE,{"derivedFrom":sQuery(id+"F4.wireOp",EDGE,"E6.0.2.2")}),1.0]])]});
            var Q13;
            Q13=makeQuery(id+"F4.imprint","IMPRINT",FACE,{"disambiguationData":[TD([[makeQuery(id+"F4.imprint","IMPRINT",EDGE,{"derivedFrom":sQuery(id+"F4.wireOp",EDGE,"E6.0.1.2")}),1.0]])]});
            var Q14;
            Q14=makeQuery(id+"F4.imprint","IMPRINT",FACE,{"disambiguationData":[TD([[makeQuery(id+"F4.imprint","IMPRINT",EDGE,{"derivedFrom":sQuery(id+"F4.wireOp",EDGE,"E5.2.0.1")}),1.0]])]});
            var Q15;
            Q15=sQuery(id+"F4.wireOp",EDGE,"E3");
            var Q16;
            Q16=sQuery(id+"F4.wireOp",EDGE,"E6.0.1.1");
            var Q17;
            Q17=sQuery(id+"F4.wireOp",EDGE,"E6.0.2.1");
            var Q18;
            Q18=sQuery(id+"F4.wireOp",EDGE,"E6.0.3.1");
            var Q19;
            Q19=sQuery(id+"F4.wireOp",EDGE,"E6.0.4.1");
            var Q20;
            Q20=sQuery(id+"F4.wireOp",EDGE,"E6.0.4.5");
            var Q21;
            Q21=sQuery(id+"F4.wireOp",EDGE,"E6.0.3.5");
            var Q22;
            Q22=sQuery(id+"F4.wireOp",EDGE,"E6.0.2.5");
            var Q23;
            Q23=sQuery(id+"F4.wireOp",EDGE,"E6.0.1.5");
            var Q24;
            Q24=sQuery(id+"F4.wireOp",EDGE,"E5.1.0.1");
            var Q25;
            Q25=sQuery(id+"F4.wireOp",EDGE,"E5.2.0.1");
            var Q26;
            Q26=sQuery(id+"F4.wireOp",EDGE,"E6.0.1.2");
            var Q27;
            Q27=sQuery(id+"F4.wireOp",EDGE,"E6.0.2.2");
            var Q28;
            Q28=sQuery(id+"F4.wireOp",EDGE,"E6.0.3.2");
            var Q29;
            Q29=sQuery(id+"F4.wireOp",EDGE,"E6.0.4.2");
            var Q30;
            Q30=makeQuery(id+"F1.opExtrude","CAP_FACE",FACE,{"disambiguationData":[OSD([sQuery(id+"F0.wireOp",EDGE,"E0.bottom"),sQuery(id+"F0.wireOp",EDGE,"E0.top"),sQuery(id+"F0.wireOp",EDGE,"E0.left"),sQuery(id+"F0.wireOp",EDGE,"E0.right")])],"isStart":true});
            extrude(context, id + "F6", {"entities" : qUnion([Q0, Q1, Q2, Q3, Q4, Q5, Q6, Q7, Q8, Q9, Q10, Q11, Q12, Q13, Q14]), "operationType" : NewBodyOperationType.REMOVE, "surfaceEntities" : qUnion([Q15, Q16, Q17, Q18, Q19, Q20, Q21, Q22, Q23, Q24, Q25, Q26, Q27, Q28, Q29]), "endBound" : BoundingType.UP_TO_SURFACE, "oppositeDirection" : true, "depth" : 25 * mm, "endBoundEntityFace" : qUnion([Q30]), "offsetDistance" : 25 * mm});
        }
        {
            var Q0;
            Q0=makeQuery(id+"F1.opExtrude","SWEPT_FACE",FACE,{"disambiguationData":[OSD([sQuery(id+"F0.wireOp",EDGE,"E0.right")])]});
            var sketch = newSketch(context, id + "F7", { "sketchPlane" : qUnion([Q0])});
            skLineSegment(sketch, "E123", {"start": v(59.77, 17) * mm, "end": v(93.6, 17) * mm});
            skLineSegment(sketch, "E124", {"start": v(101.6, 25) * mm, "end": v(101.6, 155) * mm});
            skLineSegment(sketch, "E125", {"start": v(93.6, 163) * mm, "end": v(59.77, 163) * mm});
            skLineSegment(sketch, "E126", {"start": v(51.77, 155) * mm, "end": v(51.77, 25) * mm});
            skLineSegment(sketch, "E127", {"start": v(124.6, 25) * mm, "end": v(124.6, 155) * mm});
            skLineSegment(sketch, "E128", {"start": v(132.6, 163) * mm, "end": v(167.4, 163) * mm});
            skLineSegment(sketch, "E129", {"start": v(175.4, 155) * mm, "end": v(175.4, 25) * mm});
            skLineSegment(sketch, "E130", {"start": v(167.4, 17) * mm, "end": v(132.6, 17) * mm});
            skLineSegment(sketch, "E131", {"start": v(195.4, 25) * mm, "end": v(195.4, 155) * mm});
            skLineSegment(sketch, "E132", {"start": v(203.4, 163) * mm, "end": v(238.2, 163) * mm});
            skLineSegment(sketch, "E133", {"start": v(246.2, 155) * mm, "end": v(246.2, 25) * mm});
            skLineSegment(sketch, "E134", {"start": v(238.2, 17) * mm, "end": v(203.4, 17) * mm});
            skLineSegment(sketch, "E135", {"start": v(529.2, 25) * mm, "end": v(529.2, 155) * mm});
            skLineSegment(sketch, "E136", {"start": v(521.2, 163) * mm, "end": v(489.4, 163) * mm});
            skLineSegment(sketch, "E137", {"start": v(481.4, 155) * mm, "end": v(481.4, 25) * mm});
            skLineSegment(sketch, "E138", {"start": v(489.4, 17) * mm, "end": v(521.2, 17) * mm});
            skLineSegment(sketch, "E139", {"start": v(461.4, 25) * mm, "end": v(461.4, 155) * mm});
            skLineSegment(sketch, "E140", {"start": v(453.4, 163) * mm, "end": v(418.6, 163) * mm});
            skLineSegment(sketch, "E141", {"start": v(410.6, 155) * mm, "end": v(410.6, 25) * mm});
            skLineSegment(sketch, "E142", {"start": v(418.6, 17) * mm, "end": v(453.4, 17) * mm});
            skLineSegment(sketch, "E143", {"start": v(390.6, 25) * mm, "end": v(390.6, 155) * mm});
            skLineSegment(sketch, "E144", {"start": v(382.6, 163) * mm, "end": v(347.8, 163) * mm});
            skLineSegment(sketch, "E145", {"start": v(339.8, 155) * mm, "end": v(339.8, 25) * mm});
            skLineSegment(sketch, "E146", {"start": v(347.8, 17) * mm, "end": v(382.6, 17) * mm});
            skLineSegment(sketch, "E147", {"start": v(266.2, 25) * mm, "end": v(266.2, 155) * mm});
            skLineSegment(sketch, "E148", {"start": v(319.8, 25) * mm, "end": v(319.8, 155) * mm});
            skLineSegment(sketch, "E149", {"start": v(311.8, 163) * mm, "end": v(274.2, 163) * mm});
            skLineSegment(sketch, "E150", {"start": v(274.2, 17) * mm, "end": v(311.8, 17) * mm});
            skPoint(sketch, "E151.visualSharp", {"position": v(51.77, 163) * mm});
            skArc(sketch, "E151.filletArc", {"start": v(59.77, 163) * mm, "mid": v(54.11, 160.66) * mm, "end": v(51.77, 155) * mm});
            skPoint(sketch, "E152.visualSharp", {"position": v(101.6, 163) * mm});
            skArc(sketch, "E152.filletArc", {"start": v(101.6, 155) * mm, "mid": v(99.26, 160.66) * mm, "end": v(93.6, 163) * mm});
            skPoint(sketch, "E153.visualSharp", {"position": v(51.77, 17) * mm});
            skArc(sketch, "E153.filletArc", {"start": v(51.77, 25) * mm, "mid": v(54.11, 19.34) * mm, "end": v(59.77, 17) * mm});
            skPoint(sketch, "E154.visualSharp", {"position": v(101.6, 17) * mm});
            skArc(sketch, "E154.filletArc", {"start": v(93.6, 17) * mm, "mid": v(99.26, 19.34) * mm, "end": v(101.6, 25) * mm});
            skPoint(sketch, "E155.visualSharp", {"position": v(124.6, 163) * mm});
            skArc(sketch, "E155.filletArc", {"start": v(132.6, 163) * mm, "mid": v(126.94, 160.66) * mm, "end": v(124.6, 155) * mm});
            skPoint(sketch, "E156.visualSharp", {"position": v(175.4, 163) * mm});
            skArc(sketch, "E156.filletArc", {"start": v(175.4, 155) * mm, "mid": v(173.06, 160.66) * mm, "end": v(167.4, 163) * mm});
            skPoint(sketch, "E157.visualSharp", {"position": v(124.6, 17) * mm});
            skArc(sketch, "E157.filletArc", {"start": v(124.6, 25) * mm, "mid": v(126.94, 19.34) * mm, "end": v(132.6, 17) * mm});
            skPoint(sketch, "E158.visualSharp", {"position": v(175.4, 17) * mm});
            skArc(sketch, "E158.filletArc", {"start": v(167.4, 17) * mm, "mid": v(173.06, 19.34) * mm, "end": v(175.4, 25) * mm});
            skPoint(sketch, "E159.visualSharp", {"position": v(195.4, 163) * mm});
            skArc(sketch, "E159.filletArc", {"start": v(203.4, 163) * mm, "mid": v(197.74, 160.66) * mm, "end": v(195.4, 155) * mm});
            skPoint(sketch, "E160.visualSharp", {"position": v(246.2, 163) * mm});
            skArc(sketch, "E160.filletArc", {"start": v(246.2, 155) * mm, "mid": v(243.86, 160.66) * mm, "end": v(238.2, 163) * mm});
            skPoint(sketch, "E161.visualSharp", {"position": v(195.4, 17) * mm});
            skArc(sketch, "E161.filletArc", {"start": v(195.4, 25) * mm, "mid": v(197.74, 19.34) * mm, "end": v(203.4, 17) * mm});
            skPoint(sketch, "E162.visualSharp", {"position": v(246.2, 17) * mm});
            skArc(sketch, "E162.filletArc", {"start": v(238.2, 17) * mm, "mid": v(243.86, 19.34) * mm, "end": v(246.2, 25) * mm});
            skPoint(sketch, "E163.visualSharp", {"position": v(266.2, 163) * mm});
            skArc(sketch, "E163.filletArc", {"start": v(274.2, 163) * mm, "mid": v(268.54, 160.66) * mm, "end": v(266.2, 155) * mm});
            skPoint(sketch, "E164.visualSharp", {"position": v(319.8, 163) * mm});
            skArc(sketch, "E164.filletArc", {"start": v(319.8, 155) * mm, "mid": v(317.46, 160.66) * mm, "end": v(311.8, 163) * mm});
            skPoint(sketch, "E165.visualSharp", {"position": v(266.2, 17) * mm});
            skArc(sketch, "E165.filletArc", {"start": v(266.2, 25) * mm, "mid": v(268.54, 19.34) * mm, "end": v(274.2, 17) * mm});
            skPoint(sketch, "E166.visualSharp", {"position": v(319.8, 17) * mm});
            skArc(sketch, "E166.filletArc", {"start": v(311.8, 17) * mm, "mid": v(317.46, 19.34) * mm, "end": v(319.8, 25) * mm});
            skPoint(sketch, "E167.visualSharp", {"position": v(339.8, 163) * mm});
            skArc(sketch, "E167.filletArc", {"start": v(347.8, 163) * mm, "mid": v(342.14, 160.66) * mm, "end": v(339.8, 155) * mm});
            skPoint(sketch, "E168.visualSharp", {"position": v(339.8, 17) * mm});
            skArc(sketch, "E168.filletArc", {"start": v(339.8, 25) * mm, "mid": v(342.14, 19.34) * mm, "end": v(347.8, 17) * mm});
            skPoint(sketch, "E169.visualSharp", {"position": v(390.6, 17) * mm});
            skArc(sketch, "E169.filletArc", {"start": v(382.6, 17) * mm, "mid": v(388.26, 19.34) * mm, "end": v(390.6, 25) * mm});
            skPoint(sketch, "E170.visualSharp", {"position": v(390.6, 163) * mm});
            skArc(sketch, "E170.filletArc", {"start": v(390.6, 155) * mm, "mid": v(388.26, 160.66) * mm, "end": v(382.6, 163) * mm});
            skPoint(sketch, "E171.visualSharp", {"position": v(410.6, 163) * mm});
            skArc(sketch, "E171.filletArc", {"start": v(418.6, 163) * mm, "mid": v(412.94, 160.66) * mm, "end": v(410.6, 155) * mm});
            skPoint(sketch, "E172.visualSharp", {"position": v(410.6, 17) * mm});
            skArc(sketch, "E172.filletArc", {"start": v(410.6, 25) * mm, "mid": v(412.94, 19.34) * mm, "end": v(418.6, 17) * mm});
            skPoint(sketch, "E173.visualSharp", {"position": v(461.4, 163) * mm});
            skArc(sketch, "E173.filletArc", {"start": v(461.4, 155) * mm, "mid": v(459.06, 160.66) * mm, "end": v(453.4, 163) * mm});
            skPoint(sketch, "E174.visualSharp", {"position": v(461.4, 17) * mm});
            skArc(sketch, "E174.filletArc", {"start": v(453.4, 17) * mm, "mid": v(459.06, 19.34) * mm, "end": v(461.4, 25) * mm});
            skPoint(sketch, "E175.visualSharp", {"position": v(481.4, 163) * mm});
            skArc(sketch, "E175.filletArc", {"start": v(489.4, 163) * mm, "mid": v(483.74, 160.66) * mm, "end": v(481.4, 155) * mm});
            skPoint(sketch, "E176.visualSharp", {"position": v(529.2, 163) * mm});
            skArc(sketch, "E176.filletArc", {"start": v(529.2, 155) * mm, "mid": v(526.86, 160.66) * mm, "end": v(521.2, 163) * mm});
            skPoint(sketch, "E177.visualSharp", {"position": v(481.4, 17) * mm});
            skArc(sketch, "E177.filletArc", {"start": v(481.4, 25) * mm, "mid": v(483.74, 19.34) * mm, "end": v(489.4, 17) * mm});
            skPoint(sketch, "E178.visualSharp", {"position": v(529.2, 17) * mm});
            skArc(sketch, "E178.filletArc", {"start": v(521.2, 17) * mm, "mid": v(526.86, 19.34) * mm, "end": v(529.2, 25) * mm});
            skSolve(sketch);
        }
        {
            var Q0;
            Q0=makeQuery(id+"F7.imprint","IMPRINT",FACE,{"disambiguationData":[TD([[makeQuery(id+"F7.imprint","IMPRINT",EDGE,{"derivedFrom":sQuery(id+"F7.wireOp",EDGE,"E123")}),1.0]])]});
            var Q1;
            Q1=makeQuery(id+"F7.imprint","IMPRINT",FACE,{"disambiguationData":[TD([[makeQuery(id+"F7.imprint","IMPRINT",EDGE,{"derivedFrom":sQuery(id+"F7.wireOp",EDGE,"E127")}),-1.0]])]});
            var Q2;
            Q2=makeQuery(id+"F7.imprint","IMPRINT",FACE,{"disambiguationData":[TD([[makeQuery(id+"F7.imprint","IMPRINT",EDGE,{"derivedFrom":sQuery(id+"F7.wireOp",EDGE,"E131")}),-1.0]])]});
            var Q3;
            Q3=makeQuery(id+"F7.imprint","IMPRINT",FACE,{"disambiguationData":[TD([[makeQuery(id+"F7.imprint","IMPRINT",EDGE,{"derivedFrom":sQuery(id+"F7.wireOp",EDGE,"E147")}),-1.0]])]});
            var Q4;
            Q4=makeQuery(id+"F7.imprint","IMPRINT",FACE,{"disambiguationData":[TD([[makeQuery(id+"F7.imprint","IMPRINT",EDGE,{"derivedFrom":sQuery(id+"F7.wireOp",EDGE,"E143")}),1.0]])]});
            var Q5;
            Q5=makeQuery(id+"F7.imprint","IMPRINT",FACE,{"disambiguationData":[TD([[makeQuery(id+"F7.imprint","IMPRINT",EDGE,{"derivedFrom":sQuery(id+"F7.wireOp",EDGE,"E139")}),1.0]])]});
            var Q6;
            Q6=makeQuery(id+"F7.imprint","IMPRINT",FACE,{"disambiguationData":[TD([[makeQuery(id+"F7.imprint","IMPRINT",EDGE,{"derivedFrom":sQuery(id+"F7.wireOp",EDGE,"E135")}),1.0]])]});
            var Q7;
            Q7=makeQuery(id+"F1.opExtrude","SWEPT_FACE",FACE,{"disambiguationData":[OSD([sQuery(id+"F0.wireOp",EDGE,"E0.left")])]});
            extrude(context, id + "F8", {"entities" : qUnion([Q0, Q1, Q2, Q3, Q4, Q5, Q6]), "operationType" : NewBodyOperationType.REMOVE, "endBound" : BoundingType.UP_TO_SURFACE, "oppositeDirection" : true, "depth" : 25 * mm, "endBoundEntityFace" : qUnion([Q7]), "offsetDistance" : 25 * mm});
        }
        {
            var Q0;
            Q0=makeQuery(id+"F1.opExtrude","SWEPT_FACE",FACE,{"disambiguationData":[OSD([sQuery(id+"F0.wireOp",EDGE,"E0.bottom")])]});
            var sketch = newSketch(context, id + "F9", { "sketchPlane" : qUnion([Q0])});
            skLineSegment(sketch, "E179", {"start": v(20, 25) * mm, "end": v(20, 155) * mm});
            skLineSegment(sketch, "E180", {"start": v(28, 163) * mm, "end": v(62.8, 163) * mm});
            skLineSegment(sketch, "E181", {"start": v(70.8, 155) * mm, "end": v(70.8, 25) * mm});
            skLineSegment(sketch, "E182", {"start": v(62.8, 17) * mm, "end": v(28, 17) * mm});
            skLineSegment(sketch, "E183", {"start": v(420, 25) * mm, "end": v(420, 155) * mm});
            skLineSegment(sketch, "E184", {"start": v(412, 163) * mm, "end": v(377.2, 163) * mm});
            skLineSegment(sketch, "E185", {"start": v(369.2, 155) * mm, "end": v(369.2, 25) * mm});
            skLineSegment(sketch, "E186", {"start": v(377.2, 17) * mm, "end": v(412, 17) * mm});
            skLineSegment(sketch, "E187", {"start": v(349.2, 25) * mm, "end": v(349.2, 155) * mm});
            skLineSegment(sketch, "E188", {"start": v(341.2, 163) * mm, "end": v(306.4, 163) * mm});
            skLineSegment(sketch, "E189", {"start": v(298.4, 155) * mm, "end": v(298.4, 25) * mm});
            skLineSegment(sketch, "E190", {"start": v(306.4, 17) * mm, "end": v(341.2, 17) * mm});
            skLineSegment(sketch, "E191", {"start": v(90.8, 25) * mm, "end": v(90.8, 155) * mm});
            skLineSegment(sketch, "E192", {"start": v(98.8, 163) * mm, "end": v(133.6, 163) * mm});
            skLineSegment(sketch, "E193", {"start": v(141.6, 155) * mm, "end": v(141.6, 25) * mm});
            skLineSegment(sketch, "E194", {"start": v(133.6, 17) * mm, "end": v(98.8, 17) * mm});
            skLineSegment(sketch, "E195", {"start": v(161.6, 25) * mm, "end": v(161.6, 155) * mm});
            skLineSegment(sketch, "E196", {"start": v(278.4, 25) * mm, "end": v(278.4, 155) * mm});
            skLineSegment(sketch, "E197", {"start": v(270.4, 163) * mm, "end": v(169.6, 163) * mm});
            skLineSegment(sketch, "E198", {"start": v(169.6, 17) * mm, "end": v(270.4, 17) * mm});
            skPoint(sketch, "E199.visualSharp", {"position": v(20, 163) * mm});
            skArc(sketch, "E199.filletArc", {"start": v(28, 163) * mm, "mid": v(22.34, 160.66) * mm, "end": v(20, 155) * mm});
            skPoint(sketch, "E200.visualSharp", {"position": v(70.8, 163) * mm});
            skArc(sketch, "E200.filletArc", {"start": v(70.8, 155) * mm, "mid": v(68.46, 160.66) * mm, "end": v(62.8, 163) * mm});
            skPoint(sketch, "E201.visualSharp", {"position": v(20, 17) * mm});
            skArc(sketch, "E201.filletArc", {"start": v(20, 25) * mm, "mid": v(22.34, 19.34) * mm, "end": v(28, 17) * mm});
            skPoint(sketch, "E202.visualSharp", {"position": v(70.8, 17) * mm});
            skArc(sketch, "E202.filletArc", {"start": v(62.8, 17) * mm, "mid": v(68.46, 19.34) * mm, "end": v(70.8, 25) * mm});
            skPoint(sketch, "E203.visualSharp", {"position": v(90.8, 163) * mm});
            skArc(sketch, "E203.filletArc", {"start": v(98.8, 163) * mm, "mid": v(93.14, 160.66) * mm, "end": v(90.8, 155) * mm});
            skPoint(sketch, "E204.visualSharp", {"position": v(141.6, 163) * mm});
            skArc(sketch, "E204.filletArc", {"start": v(141.6, 155) * mm, "mid": v(139.26, 160.66) * mm, "end": v(133.6, 163) * mm});
            skPoint(sketch, "E205.visualSharp", {"position": v(90.8, 17) * mm});
            skArc(sketch, "E205.filletArc", {"start": v(90.8, 25) * mm, "mid": v(93.14, 19.34) * mm, "end": v(98.8, 17) * mm});
            skPoint(sketch, "E206.visualSharp", {"position": v(141.6, 17) * mm});
            skArc(sketch, "E206.filletArc", {"start": v(133.6, 17) * mm, "mid": v(139.26, 19.34) * mm, "end": v(141.6, 25) * mm});
            skPoint(sketch, "E207.visualSharp", {"position": v(161.6, 163) * mm});
            skArc(sketch, "E207.filletArc", {"start": v(169.6, 163) * mm, "mid": v(163.94, 160.66) * mm, "end": v(161.6, 155) * mm});
            skPoint(sketch, "E208.visualSharp", {"position": v(278.4, 163) * mm});
            skArc(sketch, "E208.filletArc", {"start": v(278.4, 155) * mm, "mid": v(276.06, 160.66) * mm, "end": v(270.4, 163) * mm});
            skPoint(sketch, "E209.visualSharp", {"position": v(161.6, 17) * mm});
            skArc(sketch, "E209.filletArc", {"start": v(161.6, 25) * mm, "mid": v(163.94, 19.34) * mm, "end": v(169.6, 17) * mm});
            skPoint(sketch, "E210.visualSharp", {"position": v(278.4, 17) * mm});
            skArc(sketch, "E210.filletArc", {"start": v(270.4, 17) * mm, "mid": v(276.06, 19.34) * mm, "end": v(278.4, 25) * mm});
            skPoint(sketch, "E211.visualSharp", {"position": v(298.4, 163) * mm});
            skArc(sketch, "E211.filletArc", {"start": v(306.4, 163) * mm, "mid": v(300.74, 160.66) * mm, "end": v(298.4, 155) * mm});
            skPoint(sketch, "E212.visualSharp", {"position": v(349.2, 163) * mm});
            skArc(sketch, "E212.filletArc", {"start": v(349.2, 155) * mm, "mid": v(346.86, 160.66) * mm, "end": v(341.2, 163) * mm});
            skPoint(sketch, "E213.visualSharp", {"position": v(298.4, 17) * mm});
            skArc(sketch, "E213.filletArc", {"start": v(298.4, 25) * mm, "mid": v(300.74, 19.34) * mm, "end": v(306.4, 17) * mm});
            skPoint(sketch, "E214.visualSharp", {"position": v(349.2, 17) * mm});
            skArc(sketch, "E214.filletArc", {"start": v(341.2, 17) * mm, "mid": v(346.86, 19.34) * mm, "end": v(349.2, 25) * mm});
            skPoint(sketch, "E215.visualSharp", {"position": v(369.2, 163) * mm});
            skArc(sketch, "E215.filletArc", {"start": v(377.2, 163) * mm, "mid": v(371.54, 160.66) * mm, "end": v(369.2, 155) * mm});
            skPoint(sketch, "E216.visualSharp", {"position": v(420, 163) * mm});
            skArc(sketch, "E216.filletArc", {"start": v(420, 155) * mm, "mid": v(417.66, 160.66) * mm, "end": v(412, 163) * mm});
            skPoint(sketch, "E217.visualSharp", {"position": v(369.2, 17) * mm});
            skArc(sketch, "E217.filletArc", {"start": v(369.2, 25) * mm, "mid": v(371.54, 19.34) * mm, "end": v(377.2, 17) * mm});
            skPoint(sketch, "E218.visualSharp", {"position": v(420, 17) * mm});
            skArc(sketch, "E218.filletArc", {"start": v(412, 17) * mm, "mid": v(417.66, 19.34) * mm, "end": v(420, 25) * mm});
            skSolve(sketch);
        }
        {
            var Q0;
            Q0=makeQuery(id+"F9.imprint","IMPRINT",FACE,{"disambiguationData":[TD([[makeQuery(id+"F9.imprint","IMPRINT",EDGE,{"derivedFrom":sQuery(id+"F9.wireOp",EDGE,"E179")}),-1.0]])]});
            var Q1;
            Q1=makeQuery(id+"F9.imprint","IMPRINT",FACE,{"disambiguationData":[TD([[makeQuery(id+"F9.imprint","IMPRINT",EDGE,{"derivedFrom":sQuery(id+"F9.wireOp",EDGE,"E191")}),-1.0]])]});
            var Q2;
            Q2=makeQuery(id+"F9.imprint","IMPRINT",FACE,{"disambiguationData":[TD([[makeQuery(id+"F9.imprint","IMPRINT",EDGE,{"derivedFrom":sQuery(id+"F9.wireOp",EDGE,"E195")}),-1.0]])]});
            var Q3;
            Q3=makeQuery(id+"F9.imprint","IMPRINT",FACE,{"disambiguationData":[TD([[makeQuery(id+"F9.imprint","IMPRINT",EDGE,{"derivedFrom":sQuery(id+"F9.wireOp",EDGE,"E187")}),1.0]])]});
            var Q4;
            Q4=makeQuery(id+"F9.imprint","IMPRINT",FACE,{"disambiguationData":[TD([[makeQuery(id+"F9.imprint","IMPRINT",EDGE,{"derivedFrom":sQuery(id+"F9.wireOp",EDGE,"E183")}),1.0]])]});
            var Q5;
            Q5=makeQuery(id+"F1.opExtrude","SWEPT_FACE",FACE,{"disambiguationData":[OSD([sQuery(id+"F0.wireOp",EDGE,"E0.top")])]});
            extrude(context, id + "F10", {"entities" : qUnion([Q0, Q1, Q2, Q3, Q4]), "operationType" : NewBodyOperationType.REMOVE, "endBound" : BoundingType.UP_TO_SURFACE, "oppositeDirection" : true, "depth" : 25 * mm, "endBoundEntityFace" : qUnion([Q5]), "offsetDistance" : 25 * mm});
        }
        {
            var Q0;
            Q0=makeQuery(id+"F1.opExtrude","SWEPT_BODY",BODY,{"disambiguationData":[OSD([sQuery(id+"F0.wireOp",EDGE,"E0.bottom"),sQuery(id+"F0.wireOp",EDGE,"E0.top"),sQuery(id+"F0.wireOp",EDGE,"E0.left"),sQuery(id+"F0.wireOp",EDGE,"E0.right")])]});
            transform(context, id + "F11", {"entities" : qUnion([Q0]), "transformType" : TransformType.TRANSLATION_3D, "dx" : 0 * mm, "dy" : 0 * mm, "dz" : 0 * mm, "makeCopy" : true});
        }
        {
            var Q0;
            Q0=makeQuery(id+"F11.opPattern","COPY",BODY,{"derivedFrom":makeQuery(id+"F1.opExtrude","SWEPT_BODY",BODY,{"disambiguationData":[OSD([sQuery(id+"F0.wireOp",EDGE,"E0.bottom"),sQuery(id+"F0.wireOp",EDGE,"E0.top"),sQuery(id+"F0.wireOp",EDGE,"E0.left"),sQuery(id+"F0.wireOp",EDGE,"E0.right")])]}),"instanceName":"1"});
            deleteBodies(context, id + "F12", {"entities" : qUnion([Q0])});
        }
    });
